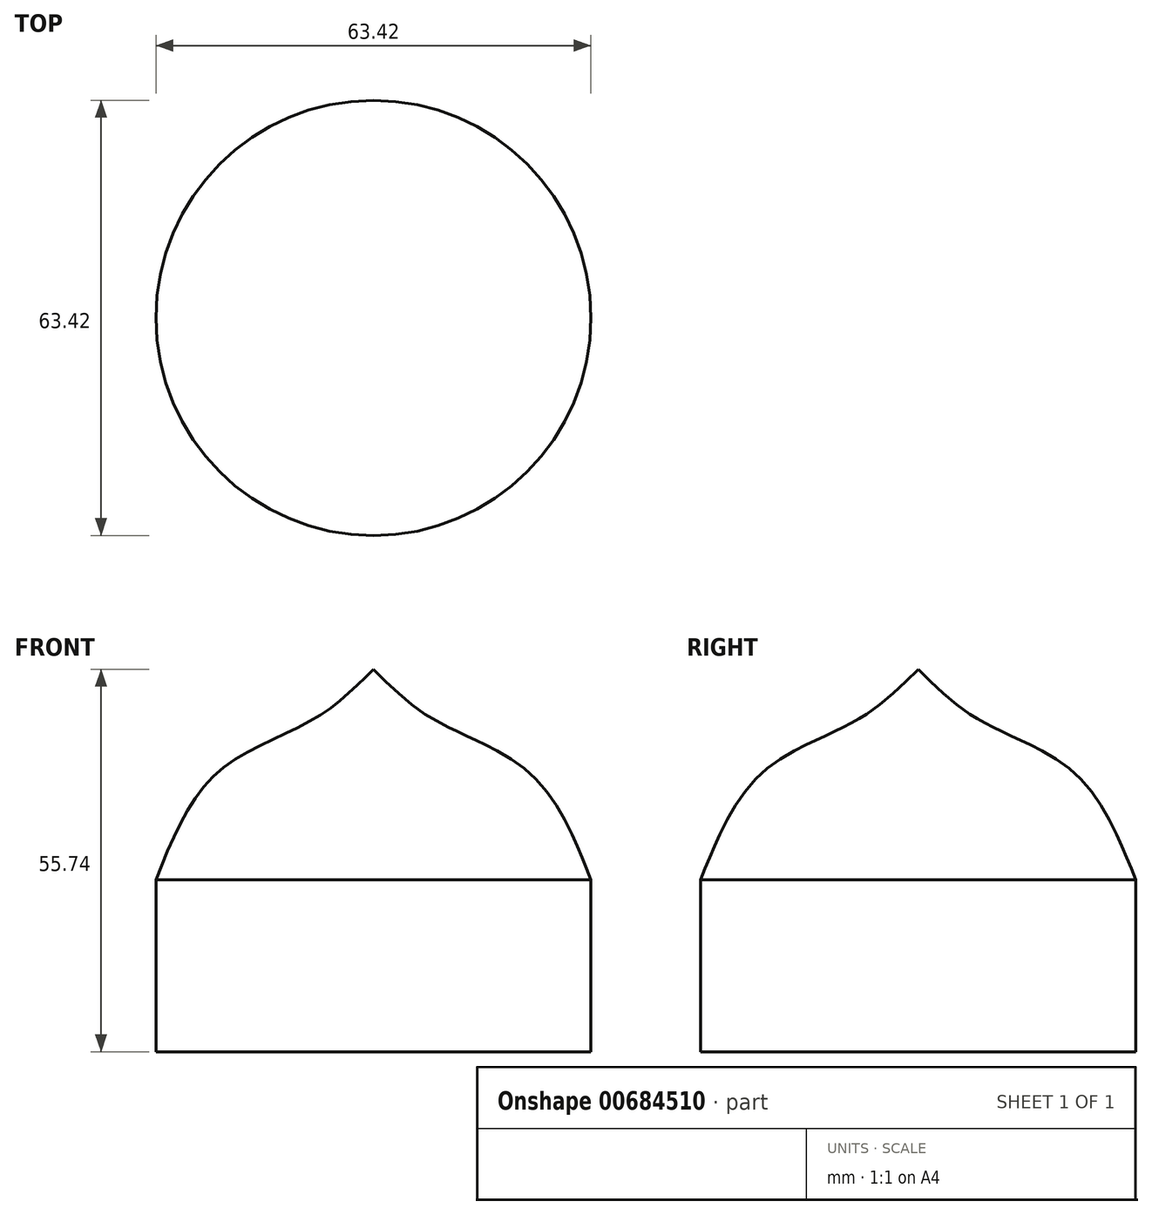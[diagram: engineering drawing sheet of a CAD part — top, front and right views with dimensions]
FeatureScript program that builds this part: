
annotation { "Feature Type Name" : "Feature", "Feature Type Description" : "" }
export const myFeature = defineFeature(function(context is Context, id is Id, definition is map)
    precondition{}
    {
        {
            var Q0;
            Q0=qCreatedBy(makeId("Front.planeOp"),FACE);
            var sketch = newSketch(context, id + "F0", { "sketchPlane" : qUnion([Q0])});
            skLineSegment(sketch, "E0", {"start": v(0, 0) * mm, "end": v(-31.7, 0) * mm});
            skLineSegment(sketch, "E1", {"start": v(-31.7, 0) * mm, "end": v(-31.7, 25.07) * mm});
            skFitSpline(sketch, "E2", {"points": [v(-31.7, 25.07) * mm, v(-22.78, 40.63) * mm, v(-8.81, 48.42) * mm, v(0, 55.74) * mm], "startDerivative": vector(19.29, 48.42) * mm, "endDerivative": vector(26.76, 26.96) * mm});
            skLineSegment(sketch, "E3", {"start": v(0, 55.74) * mm, "end": v(0, 0) * mm});
            skSolve(sketch);
        }
        {
            var Q0;
            Q0=makeQuery(id+"F0.imprint","IMPRINT",FACE,{"disambiguationData":[TD([[makeQuery(id+"F0.imprint","IMPRINT",EDGE,{"derivedFrom":sQuery(id+"F0.wireOp",EDGE,"E0")}),-1.0]])]});
            var Q1;
            Q1=sQuery(id+"F0.wireOp",EDGE,"E3");
            revolve(context, id + "F1", {"entities" : qUnion([Q0]), "axis" : qUnion([Q1]), "revolveType" : RevolveType.FULL});
        }
    });
